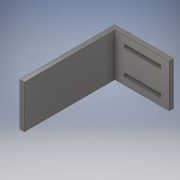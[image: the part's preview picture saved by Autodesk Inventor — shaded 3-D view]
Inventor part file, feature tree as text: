
AUTODESK INVENTOR PART (.ipt)
format: ipt  version: 2018 (Build 220112000, 112)  size: 155,648 bytes
history: native  units: in
note: dims shown in document units (in); Inventor stores cm internally (conversion verified against a paired STEP export)
features: sketch x6, extrude x5, hole x1
ambient origin geometry x8: Origin, YZ Plane, XZ Plane, XY Plane, X Axis, Y Axis, Z Axis, Center Point
bodies: Solid1 (feature_tree)
feature tree (12):
  extrude  "Extrusion1"  Depth=4.75in
  extrude  "Extrusion2"  Depth=0.5in
  sketch  "Sketch5"  dims[d5=10.0in d6=0.0in d20=4.0in]
  sketch  "Sketch7"  dims[d21=0.375in]
  hole  "Hole1"  [1 undecoded]
  extrude  "Extrusion7"  Depth=0.25in TaperAngle=0.0deg
  extrude  "Extrusion8"  Depth=2.0in
  extrude  "Extrusion9"  Depth=2.0in
  sketch  "Sketch1"  dims[d0=6.5in d1=4.75in]
  sketch  "Sketch2"  dims[d2=0.5in d3=0.0in d4=0.5in]
  sketch  "Sketch8"  dims[d24=0.375in d25=0.75in d26=0.375in d27=0.25in d28=0.5635in d29=1.0in d30=0.8108in d31=1.0in d32=0.0in]
  sketch  "Sketch9"  dims[d33=0.1875in d34=0.1875in d35=0.675in d36=0.865in d37=0.865in d38=0.25in d39=0.25in d40=1.5in d41=0.0in d42=0.75in d43=0.5in d44=2.0in d45=0.0in]
note: 1 required parameter value undecoded (feature->parameter linkage not recoverable at this tier; creation-order binding heuristic only, values carry confidence <= 0.55)
